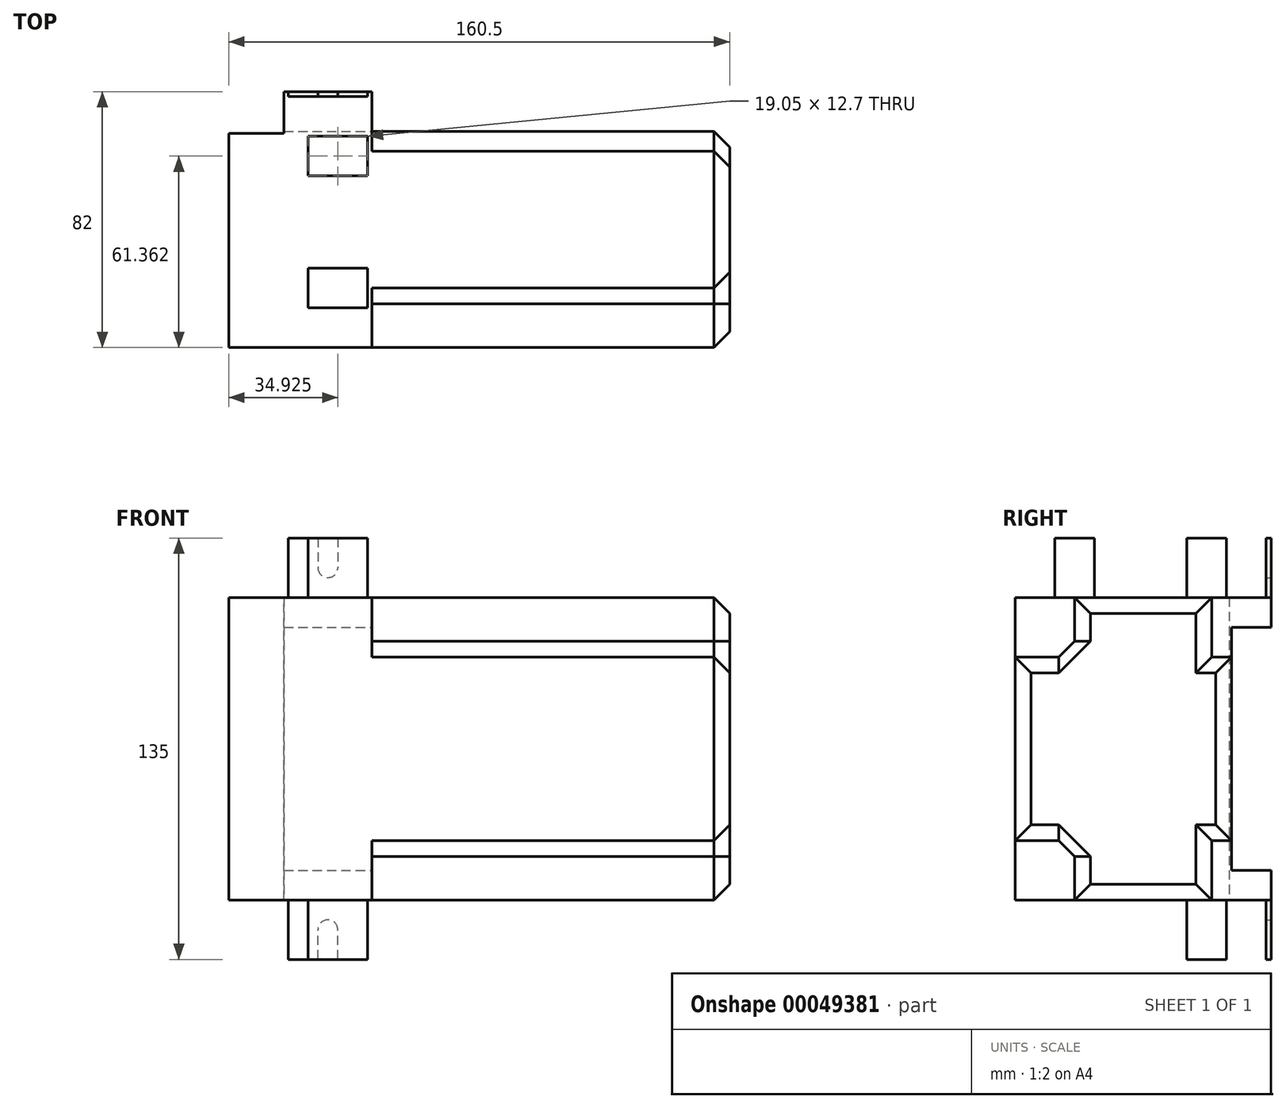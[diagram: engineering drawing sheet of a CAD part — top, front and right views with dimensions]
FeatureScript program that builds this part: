
annotation { "Feature Type Name" : "Feature", "Feature Type Description" : "" }
export const myFeature = defineFeature(function(context is Context, id is Id, definition is map)
    precondition{}
    {
        {
            var Q0;
            Q0=qCreatedBy(makeId("Top.planeOp"),FACE);
            var sketch = newSketch(context, id + "F0", { "sketchPlane" : qUnion([Q0])});
            skLineSegment(sketch, "E0.bottom", {"start": v(0, 0) * mm, "end": v(160.5, 0) * mm});
            skLineSegment(sketch, "E0.top", {"start": v(0, 82) * mm, "end": v(160.5, 82) * mm});
            skLineSegment(sketch, "E0.left", {"start": v(0, 0) * mm, "end": v(0, 82) * mm});
            skLineSegment(sketch, "E0.right", {"start": v(160.5, 0) * mm, "end": v(160.5, 82) * mm});
            skSolve(sketch);
        }
        {
            var Q0;
            Q0 = qSketchRegion(id + "F0", true);
            extrude(context, id + "F1", {"entities" : qUnion([Q0]), "depth" : 135 * mm});
        }
        {
            var Q0;
            Q0=makeQuery(id+"F1.opExtrude","SWEPT_FACE",FACE,{"disambiguationData":[OSD([sQuery(id+"F0.wireOp",EDGE,"E0.right")])]});
            var sketch = newSketch(context, id + "F2", { "sketchPlane" : qUnion([Q0])});
            skLineSegment(sketch, "E1.bottom", {"start": v(0, 135) * mm, "end": v(12.7, 135) * mm});
            skLineSegment(sketch, "E1.top", {"start": v(0, 115.95) * mm, "end": v(12.7, 115.95) * mm});
            skLineSegment(sketch, "E1.left", {"start": v(0, 135) * mm, "end": v(0, 115.95) * mm});
            skLineSegment(sketch, "E1.right", {"start": v(12.7, 135) * mm, "end": v(12.7, 115.95) * mm});
            skLineSegment(sketch, "E2.bottom", {"start": v(25.4, 135) * mm, "end": v(55.01, 135) * mm});
            skLineSegment(sketch, "E2.top", {"start": v(25.4, 115.95) * mm, "end": v(55.01, 115.95) * mm});
            skLineSegment(sketch, "E2.left", {"start": v(25.4, 135) * mm, "end": v(25.4, 115.95) * mm});
            skLineSegment(sketch, "E2.right", {"start": v(55.01, 135) * mm, "end": v(55.01, 115.95) * mm});
            skLineSegment(sketch, "E3.bottom", {"start": v(80.41, 135) * mm, "end": v(67.71, 135) * mm});
            skLineSegment(sketch, "E3.top", {"start": v(80.41, 115.95) * mm, "end": v(67.71, 115.95) * mm});
            skLineSegment(sketch, "E3.left", {"start": v(80.41, 135) * mm, "end": v(80.41, 115.95) * mm});
            skLineSegment(sketch, "E3.right", {"start": v(67.71, 135) * mm, "end": v(67.71, 115.95) * mm});
            skLineSegment(sketch, "E4.bottom", {"start": v(80.41, 0) * mm, "end": v(67.71, 0) * mm});
            skLineSegment(sketch, "E4.top", {"start": v(80.41, 19.05) * mm, "end": v(67.71, 19.05) * mm});
            skLineSegment(sketch, "E4.left", {"start": v(80.41, 0) * mm, "end": v(80.41, 19.05) * mm});
            skLineSegment(sketch, "E4.right", {"start": v(67.71, 0) * mm, "end": v(67.71, 19.05) * mm});
            skLineSegment(sketch, "E5.bottom", {"start": v(55.01, 0) * mm, "end": v(0, 0) * mm});
            skLineSegment(sketch, "E5.top", {"start": v(55.01, 19.05) * mm, "end": v(0, 19.05) * mm});
            skLineSegment(sketch, "E5.left", {"start": v(55.01, 0) * mm, "end": v(55.01, 19.05) * mm});
            skLineSegment(sketch, "E5.right", {"start": v(0, 0) * mm, "end": v(0, 19.05) * mm});
            skSolve(sketch);
        }
        {
            var Q0;
            Q0 = qSketchRegion(id + "F2", true);
            extrude(context, id + "F3", {"entities" : qUnion([Q0]), "operationType" : NewBodyOperationType.REMOVE, "endBound" : BoundingType.THROUGH_ALL, "oppositeDirection" : true, "depth" : 25.4 * mm});
        }
        {
            var Q0;
            Q0=makeQuery(id+"F1.opExtrude","SWEPT_FACE",FACE,{"disambiguationData":[OSD([sQuery(id+"F0.wireOp",EDGE,"E0.top")])]});
            var sketch = newSketch(context, id + "F4", { "sketchPlane" : qUnion([Q0])});
            skLineSegment(sketch, "E6.bottom", {"start": v(-160.5, 135) * mm, "end": v(-44.45, 135) * mm});
            skLineSegment(sketch, "E6.top", {"start": v(-160.5, 115.95) * mm, "end": v(-44.45, 115.95) * mm});
            skLineSegment(sketch, "E6.left", {"start": v(-160.5, 135) * mm, "end": v(-160.5, 115.95) * mm});
            skLineSegment(sketch, "E6.right", {"start": v(-44.45, 135) * mm, "end": v(-44.45, 115.95) * mm});
            skLineSegment(sketch, "E7.bottom", {"start": v(0, 135) * mm, "end": v(-19.05, 135) * mm});
            skLineSegment(sketch, "E7.top", {"start": v(0, 115.95) * mm, "end": v(-19.05, 115.95) * mm});
            skLineSegment(sketch, "E7.left", {"start": v(0, 135) * mm, "end": v(0, 115.95) * mm});
            skLineSegment(sketch, "E7.right", {"start": v(-19.05, 135) * mm, "end": v(-19.05, 115.95) * mm});
            skLineSegment(sketch, "E8.bottom", {"start": v(0, 106.43) * mm, "end": v(-160.5, 106.42) * mm});
            skLineSegment(sketch, "E9.bottom", {"start": v(-34.93, 135) * mm, "end": v(-28.58, 135) * mm});
            skLineSegment(sketch, "E9.left", {"start": v(-34.93, 135) * mm, "end": v(-34.93, 125.48) * mm});
            skLineSegment(sketch, "E9.right", {"start": v(-28.58, 135) * mm, "end": v(-28.58, 125.48) * mm});
            skLineSegment(sketch, "E10", {"start": v(-160.5, 67.5) * mm, "end": v(0, 67.5) * mm, "construction": true});
            skLineSegment(sketch, "E11", {"start": v(-160.5, 106.42) * mm, "end": v(-160.5, 67.5) * mm});
            skLineSegment(sketch, "E12", {"start": v(0, 67.5) * mm, "end": v(0, 106.43) * mm});
            skArc(sketch, "E13", {"start": v(-34.93, 125.48) * mm, "mid": v(-31.75, 122.3) * mm, "end": v(-28.58, 125.48) * mm});
            skLineSegment(sketch, "E14", {"start": v(-160.5, 67.5) * mm, "end": v(0, 67.5) * mm});
            skArc(sketch, "E15.MirrorCS", {"start": v(-34.93, 9.53) * mm, "mid": v(-31.75, 12.7) * mm, "end": v(-28.58, 9.53) * mm});
            skLineSegment(sketch, "E16.MirrorCS", {"start": v(-28.58, 0) * mm, "end": v(-28.58, 9.53) * mm});
            skLineSegment(sketch, "E17.MirrorCS", {"start": v(-34.93, 0) * mm, "end": v(-34.93, 9.53) * mm});
            skLineSegment(sketch, "E18.MirrorCS", {"start": v(-34.93, 0) * mm, "end": v(-28.58, 0) * mm});
            skLineSegment(sketch, "E19.MirrorCS", {"start": v(0, 67.5) * mm, "end": v(0, 28.58) * mm});
            skLineSegment(sketch, "E20.MirrorCS", {"start": v(-160.5, 0) * mm, "end": v(-44.45, 0) * mm});
            skLineSegment(sketch, "E21.MirrorCS", {"start": v(-160.5, 19.05) * mm, "end": v(-44.45, 19.05) * mm});
            skLineSegment(sketch, "E22.MirrorCS", {"start": v(-160.5, 0) * mm, "end": v(-160.5, 19.05) * mm});
            skLineSegment(sketch, "E23.MirrorCS", {"start": v(-44.45, 0) * mm, "end": v(-44.45, 19.05) * mm});
            skLineSegment(sketch, "E24.MirrorCS", {"start": v(-160.5, 28.58) * mm, "end": v(-160.5, 67.5) * mm});
            skLineSegment(sketch, "E25.MirrorCS", {"start": v(-19.05, 0) * mm, "end": v(-19.05, 19.05) * mm});
            skLineSegment(sketch, "E26.MirrorCS", {"start": v(0, 28.58) * mm, "end": v(-160.5, 28.58) * mm});
            skLineSegment(sketch, "E27.MirrorCS", {"start": v(0, 0) * mm, "end": v(0, 19.05) * mm});
            skLineSegment(sketch, "E28.MirrorCS", {"start": v(0, 19.05) * mm, "end": v(-19.05, 19.05) * mm});
            skLineSegment(sketch, "E29.MirrorCS", {"start": v(0, 0) * mm, "end": v(-19.05, 0) * mm});
            skSolve(sketch);
        }
        {
            var Q0;
            Q0 = qSketchRegion(id + "F4", true);
            extrude(context, id + "F5", {"entities" : qUnion([Q0]), "operationType" : NewBodyOperationType.REMOVE, "oppositeDirection" : true, "depth" : 12.7 * mm});
        }
        {
            var Q0;
            Q0=makeQuery(id+"F1.opExtrude","SWEPT_FACE",FACE,{"disambiguationData":[OSD([sQuery(id+"F0.wireOp",EDGE,"E0.bottom")])]});
            var sketch = newSketch(context, id + "F6", { "sketchPlane" : qUnion([Q0])});
            skLineSegment(sketch, "E30.bottom", {"start": v(0, 115.95) * mm, "end": v(25.4, 115.95) * mm});
            skLineSegment(sketch, "E30.top", {"start": v(0, 135) * mm, "end": v(25.4, 135) * mm});
            skLineSegment(sketch, "E30.left", {"start": v(0, 115.95) * mm, "end": v(0, 135) * mm});
            skLineSegment(sketch, "E30.right", {"start": v(25.4, 115.95) * mm, "end": v(25.4, 135) * mm});
            skLineSegment(sketch, "E31.bottom", {"start": v(160.5, 115.95) * mm, "end": v(44.45, 115.95) * mm});
            skLineSegment(sketch, "E31.top", {"start": v(160.5, 135) * mm, "end": v(44.45, 135) * mm});
            skLineSegment(sketch, "E31.left", {"start": v(160.5, 115.95) * mm, "end": v(160.5, 135) * mm});
            skLineSegment(sketch, "E31.right", {"start": v(44.45, 115.95) * mm, "end": v(44.45, 135) * mm});
            skLineSegment(sketch, "E32.bottom", {"start": v(0, 0) * mm, "end": v(25.4, 0) * mm});
            skLineSegment(sketch, "E32.top", {"start": v(0, 19.05) * mm, "end": v(25.4, 19.05) * mm});
            skLineSegment(sketch, "E32.left", {"start": v(0, 0) * mm, "end": v(0, 19.05) * mm});
            skLineSegment(sketch, "E32.right", {"start": v(25.4, 0) * mm, "end": v(25.4, 19.05) * mm});
            skLineSegment(sketch, "E33.bottom", {"start": v(44.45, 19.05) * mm, "end": v(160.5, 19.05) * mm});
            skLineSegment(sketch, "E33.top", {"start": v(44.45, 0) * mm, "end": v(160.5, 0) * mm});
            skLineSegment(sketch, "E33.left", {"start": v(44.45, 19.05) * mm, "end": v(44.45, 0) * mm});
            skLineSegment(sketch, "E33.right", {"start": v(160.5, 19.05) * mm, "end": v(160.5, 0) * mm});
            skSolve(sketch);
        }
        {
            var Q0;
            Q0=makeQuery(id+"F6.imprint","IMPRINT",FACE,{"disambiguationData":[TD([[makeQuery(id+"F6.imprint","IMPRINT",EDGE,{"derivedFrom":sQuery(id+"F6.wireOp",EDGE,"E30.bottom")}),1.0]])]});
            var Q1;
            Q1=makeQuery(id+"F6.imprint","IMPRINT",FACE,{"disambiguationData":[TD([[makeQuery(id+"F6.imprint","IMPRINT",EDGE,{"derivedFrom":sQuery(id+"F6.wireOp",EDGE,"E31.bottom")}),1.0]])]});
            var Q2;
            Q2=makeQuery(id+"F6.imprint","IMPRINT",FACE,{"disambiguationData":[TD([[makeQuery(id+"F6.imprint","IMPRINT",EDGE,{"derivedFrom":sQuery(id+"F6.wireOp",EDGE,"E32.bottom")}),1.0]])]});
            var Q3;
            Q3=makeQuery(id+"F6.imprint","IMPRINT",FACE,{"disambiguationData":[TD([[makeQuery(id+"F6.imprint","IMPRINT",EDGE,{"derivedFrom":sQuery(id+"F6.wireOp",EDGE,"E33.bottom")}),-1.0]])]});
            extrude(context, id + "F7", {"entities" : qUnion([Q0, Q1, Q2, Q3]), "operationType" : NewBodyOperationType.REMOVE, "oppositeDirection" : true, "depth" : 74.34 * mm});
        }
        {
            var Q0;
            Q0=makeQuery(id+"F1.opExtrude","SWEPT_FACE",FACE,{"disambiguationData":[OSD([sQuery(id+"F0.wireOp",EDGE,"E0.right")])]});
            var sketch = newSketch(context, id + "F8", { "sketchPlane" : qUnion([Q0])});
            skLineSegment(sketch, "E34.bottom", {"start": v(0, 115.95) * mm, "end": v(19.05, 115.95) * mm});
            skLineSegment(sketch, "E34.top", {"start": v(0, 96.9) * mm, "end": v(19.05, 96.9) * mm});
            skLineSegment(sketch, "E34.left", {"start": v(0, 115.95) * mm, "end": v(0, 96.9) * mm});
            skLineSegment(sketch, "E34.right", {"start": v(19.05, 115.95) * mm, "end": v(19.05, 96.9) * mm});
            skLineSegment(sketch, "E35.bottom", {"start": v(82, 115.95) * mm, "end": v(62.95, 115.95) * mm});
            skLineSegment(sketch, "E35.top", {"start": v(82, 96.9) * mm, "end": v(62.95, 96.9) * mm});
            skLineSegment(sketch, "E35.left", {"start": v(82, 115.95) * mm, "end": v(82, 96.9) * mm});
            skLineSegment(sketch, "E35.right", {"start": v(62.95, 115.95) * mm, "end": v(62.95, 96.9) * mm});
            skLineSegment(sketch, "E36.bottom", {"start": v(82, 19.05) * mm, "end": v(62.95, 19.05) * mm});
            skLineSegment(sketch, "E36.top", {"start": v(82, 38.1) * mm, "end": v(62.95, 38.1) * mm});
            skLineSegment(sketch, "E36.left", {"start": v(82, 19.05) * mm, "end": v(82, 38.1) * mm});
            skLineSegment(sketch, "E36.right", {"start": v(62.95, 19.05) * mm, "end": v(62.95, 38.1) * mm});
            skLineSegment(sketch, "E37.bottom", {"start": v(0, 19.05) * mm, "end": v(19.05, 19.05) * mm});
            skLineSegment(sketch, "E37.top", {"start": v(0, 38.1) * mm, "end": v(19.05, 38.1) * mm});
            skLineSegment(sketch, "E37.left", {"start": v(0, 19.05) * mm, "end": v(0, 38.1) * mm});
            skLineSegment(sketch, "E37.right", {"start": v(19.05, 19.05) * mm, "end": v(19.05, 38.1) * mm});
            skSolve(sketch);
        }
        {
            var Q0;
            Q0 = qSketchRegion(id + "F8", true);
            extrude(context, id + "F9", {"entities" : qUnion([Q0]), "operationType" : NewBodyOperationType.REMOVE, "oppositeDirection" : true, "depth" : 114.6 * mm});
        }
        {
            var Q0;
            Q0=makeQuery(id+"F9.boolean.opBoolean","COPY",EDGE,{"derivedFrom":makeQuery(id+"F9.opExtrude","SWEPT_EDGE",EDGE,{"disambiguationData":[OSD([sQuery(id+"F8.wireOp",EDGE,"E34.top"),sQuery(id+"F8.wireOp",EDGE,"E34.right")])]})});
            var Q1;
            Q1=makeQuery(id+"F9.boolean.opBoolean","COPY",EDGE,{"derivedFrom":makeQuery(id+"F9.opExtrude","SWEPT_EDGE",EDGE,{"disambiguationData":[OSD([sQuery(id+"F0.wireOp",EDGE,"E0.bottom"),sQuery(id+"F0.wireOp",EDGE,"E0.right"),sQuery(id+"F8.wireOp",EDGE,"E34.top"),sQuery(id+"F8.wireOp",EDGE,"E34.left")])]})});
            var Q2;
            Q2=makeQuery(id+"F9.boolean.opBoolean","COPY",EDGE,{"derivedFrom":makeQuery(id+"F9.opExtrude","SWEPT_EDGE",EDGE,{"disambiguationData":[OSD([sQuery(id+"F0.wireOp",EDGE,"E0.bottom"),sQuery(id+"F0.wireOp",EDGE,"E0.top"),sQuery(id+"F0.wireOp",EDGE,"E0.right"),sQuery(id+"F2.wireOp",EDGE,"E1.top"),sQuery(id+"F2.wireOp",EDGE,"E2.top"),sQuery(id+"F2.wireOp",EDGE,"E3.top"),sQuery(id+"F4.wireOp",EDGE,"E6.top"),sQuery(id+"F4.wireOp",EDGE,"E6.left"),sQuery(id+"F6.wireOp",EDGE,"E31.bottom"),sQuery(id+"F6.wireOp",EDGE,"E31.left"),sQuery(id+"F8.wireOp",EDGE,"E34.bottom"),sQuery(id+"F8.wireOp",EDGE,"E34.right")])]})});
            var Q3;
            {var subQ0=sQuery(id+"F0.wireOp",EDGE,"E0.right");Q3=makeQuery(id+"F7.boolean.opBoolean","MERGE",EDGE,{"derivedFrom":[makeQuery(id+"F3.boolean.opBoolean","COPY",EDGE,{"derivedFrom":makeQuery(id+"F3.opExtrude","CAP_EDGE",EDGE,{"disambiguationData":[OSD([sQuery(id+"F2.wireOp",EDGE,"E1.top")])],"isStart":true})}),makeQuery(id+"F3.boolean.opBoolean","COPY",EDGE,{"derivedFrom":makeQuery(id+"F3.opExtrude","CAP_EDGE",EDGE,{"disambiguationData":[OSD([sQuery(id+"F2.wireOp",EDGE,"E2.top")])],"isStart":true})}),makeQuery(id+"F5.boolean.opBoolean","MERGE",EDGE,{"derivedFrom":[makeQuery(id+"F3.boolean.opBoolean","COPY",EDGE,{"derivedFrom":makeQuery(id+"F3.opExtrude","CAP_EDGE",EDGE,{"disambiguationData":[OSD([sQuery(id+"F2.wireOp",EDGE,"E3.top")])],"isStart":true})}),makeQuery(id+"F5.opExtrude","SWEPT_EDGE",EDGE,{"disambiguationData":[OSD([sQuery(id+"F0.wireOp",EDGE,"E0.top"),subQ0,sQuery(id+"F4.wireOp",EDGE,"E6.top"),sQuery(id+"F4.wireOp",EDGE,"E6.left")])]})]}),makeQuery(id+"F7.opExtrude","SWEPT_EDGE",EDGE,{"disambiguationData":[OSD([sQuery(id+"F0.wireOp",EDGE,"E0.bottom"),subQ0,sQuery(id+"F6.wireOp",EDGE,"E31.bottom"),sQuery(id+"F6.wireOp",EDGE,"E31.left")])]})]});}
            var Q4;
            Q4=makeQuery(id+"F1.opExtrude","SWEPT_FACE",FACE,{"disambiguationData":[OSD([sQuery(id+"F0.wireOp",EDGE,"E0.right")])]});
            var Q5;
            Q5=makeQuery(id+"F9.boolean.opBoolean","COPY",EDGE,{"derivedFrom":makeQuery(id+"F9.opExtrude","SWEPT_EDGE",EDGE,{"disambiguationData":[OSD([sQuery(id+"F8.wireOp",EDGE,"E37.top"),sQuery(id+"F8.wireOp",EDGE,"E37.right")])]})});
            var Q6;
            Q6=makeQuery(id+"F9.boolean.opBoolean","COPY",EDGE,{"derivedFrom":makeQuery(id+"F9.opExtrude","SWEPT_EDGE",EDGE,{"disambiguationData":[OSD([sQuery(id+"F0.wireOp",EDGE,"E0.bottom"),sQuery(id+"F0.wireOp",EDGE,"E0.right"),sQuery(id+"F8.wireOp",EDGE,"E37.top"),sQuery(id+"F8.wireOp",EDGE,"E37.left")])]})});
            var Q7;
            Q7=makeQuery(id+"F9.boolean.opBoolean","COPY",EDGE,{"derivedFrom":makeQuery(id+"F9.opExtrude","SWEPT_EDGE",EDGE,{"disambiguationData":[OSD([sQuery(id+"F0.wireOp",EDGE,"E0.bottom"),sQuery(id+"F0.wireOp",EDGE,"E0.top"),sQuery(id+"F0.wireOp",EDGE,"E0.right"),sQuery(id+"F2.wireOp",EDGE,"E4.top"),sQuery(id+"F2.wireOp",EDGE,"E5.top"),sQuery(id+"F4.wireOp",EDGE,"E21.MirrorCS"),sQuery(id+"F4.wireOp",EDGE,"E22.MirrorCS"),sQuery(id+"F6.wireOp",EDGE,"E33.bottom"),sQuery(id+"F6.wireOp",EDGE,"E33.right"),sQuery(id+"F8.wireOp",EDGE,"E37.bottom"),sQuery(id+"F8.wireOp",EDGE,"E37.right")])]})});
            chamfer(context, id + "F10", {"entities" : qUnion([Q0, Q1, Q2, Q3, Q4, Q5, Q6, Q7]), "width" : 5.08 * mm, "tangentPropagation" : true});
        }
        {
            var Q0;
            Q0=makeQuery(id+"F1.opExtrude","SWEPT_FACE",FACE,{"disambiguationData":[OSD([sQuery(id+"F0.wireOp",EDGE,"E0.left")])]});
            var sketch = newSketch(context, id + "F11", { "sketchPlane" : qUnion([Q0])});
            skLineSegment(sketch, "E38.bottom", {"start": v(-97.27, 132.39) * mm, "end": v(-68.57, 132.39) * mm});
            skLineSegment(sketch, "E38.top", {"start": v(-97.27, -10.43) * mm, "end": v(-68.57, -10.43) * mm});
            skLineSegment(sketch, "E38.left", {"start": v(-97.27, 132.39) * mm, "end": v(-97.27, -10.43) * mm});
            skLineSegment(sketch, "E38.right", {"start": v(-68.57, 132.39) * mm, "end": v(-68.57, -10.43) * mm});
            skSolve(sketch);
        }
        {
            var Q0;
            Q0 = qSketchRegion(id + "F11", true);
            extrude(context, id + "F12", {"entities" : qUnion([Q0]), "operationType" : NewBodyOperationType.REMOVE, "oppositeDirection" : true, "depth" : 17.66 * mm});
        }
    });
